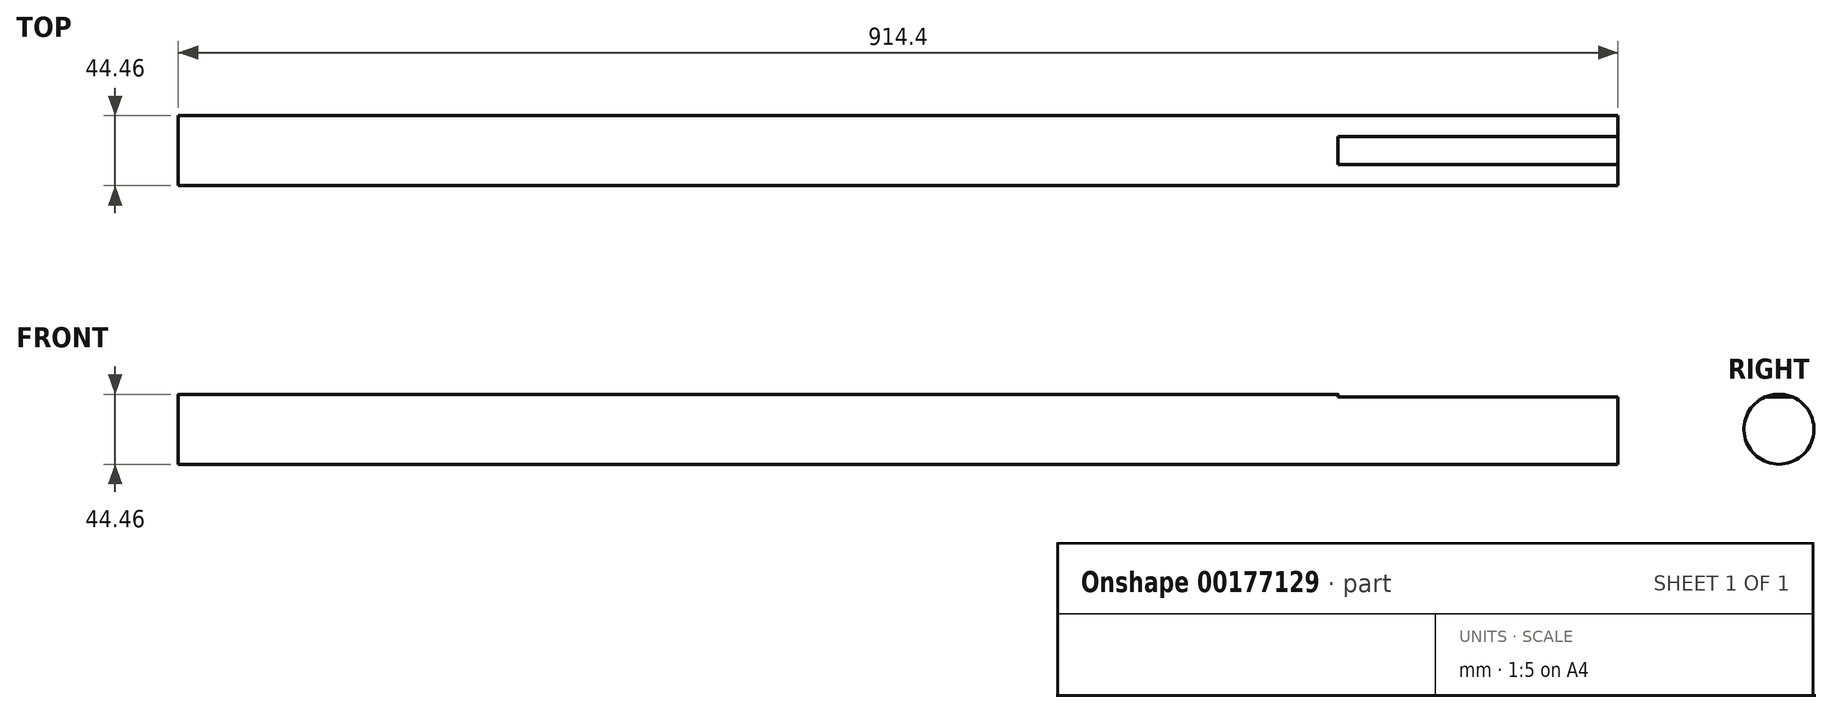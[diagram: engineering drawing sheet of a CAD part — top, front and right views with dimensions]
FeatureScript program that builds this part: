
annotation { "Feature Type Name" : "Feature", "Feature Type Description" : "" }
export const myFeature = defineFeature(function(context is Context, id is Id, definition is map)
    precondition{}
    {
        {
            var Q0;
            Q0=qCreatedBy(makeId("Right.planeOp"),FACE);
            var sketch = newSketch(context, id + "F0", { "sketchPlane" : qUnion([Q0])});
            skCircle(sketch, "E0", {"center": v(0, 0) * mm, "radius": 22.23 * mm});
            skSolve(sketch);
        }
        {
            var Q0;
            Q0=makeQuery(id+"F0.imprint","IMPRINT",FACE,{"disambiguationData":[TD([[makeQuery(id+"F0.imprint","IMPRINT",EDGE,{"derivedFrom":sQuery(id+"F0.wireOp",EDGE,"E0")}),1.0]])]});
            extrude(context, id + "F1", {"entities" : qUnion([Q0]), "depth" : 914.4 * mm});
        }
        {
            var Q0;
            Q0=makeQuery(id+"F1.opExtrude","CAP_FACE",FACE,{"disambiguationData":[OSD([sQuery(id+"F0.wireOp",EDGE,"E0")])],"isStart":false});
            var sketch = newSketch(context, id + "F2", { "sketchPlane" : qUnion([Q0])});
            skLineSegment(sketch, "E1", {"start": v(20.37, -8.9) * mm, "end": v(20.37, 8.9) * mm});
            skArc(sketch, "E2", {"start": v(20.37, 8.89) * mm, "mid": v(22.23, 0) * mm, "end": v(20.37, -8.89) * mm});
            skSolve(sketch);
        }
        {
            var Q0;
            Q0=makeQuery(id+"F2.imprint","IMPRINT",FACE,{"disambiguationData":[TD([[makeQuery(id+"F2.imprint","IMPRINT",EDGE,{"derivedFrom":sQuery(id+"F2.wireOp",EDGE,"E1")}),-1.0]])]});
            extrude(context, id + "F3", {"entities" : qUnion([Q0]), "operationType" : NewBodyOperationType.REMOVE, "oppositeDirection" : true, "depth" : 177.8 * mm});
        }
        {
            var Q0;
            Q0=makeQuery(id+"F1.opExtrude","SWEPT_BODY",BODY,{"disambiguationData":[OSD([sQuery(id+"F0.wireOp",EDGE,"E0")])]});
            var Q1;
            Q1=makeQuery(id+"F1.opExtrude","CAP_EDGE",EDGE,{"disambiguationData":[OSD([sQuery(id+"F0.wireOp",EDGE,"E0")])],"isStart":true});
            transform(context, id + "F4", {"entities" : qUnion([Q0]), "transformType" : TransformType.ROTATION, "transformAxis" : qUnion([Q1]), "angle" : 90 * degree, "makeCopy" : false});
        }
    });
